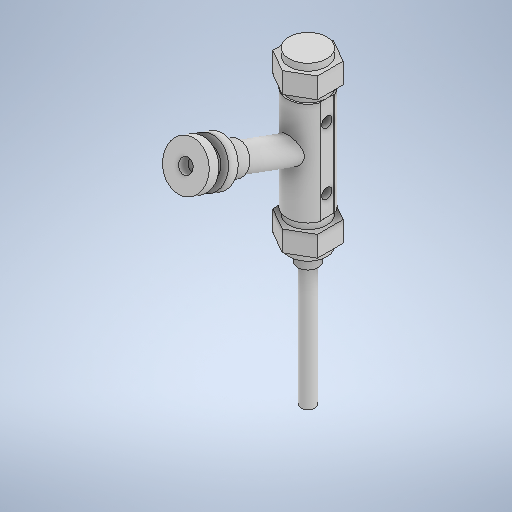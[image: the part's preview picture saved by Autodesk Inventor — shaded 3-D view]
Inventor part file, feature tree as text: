
AUTODESK INVENTOR PART (.ipt)
format: ipt  version: 2025.1 (Build 291241000, 241)  size: 469,504 bytes
history: native  units: mm
features: extrude x17, sketch x16, plane x13, other x6, hole x3, projected_geometry x3, mirror x2, shell x1, sweep x1, split x1, surface_op x1
ambient origin geometry x8: Origin, YZ Plane, XZ Plane, XY Plane, X Axis, Y Axis, Z Axis, Center Point
bodies: Volumenkörper1 (feature_tree), Solid3 (feature_tree), Solid4 (feature_tree), Solid5 (feature_tree), Solid6 (feature_tree), Solid7 (feature_tree), Solid8 (feature_tree), Solid9 (feature_tree), Solid10 (feature_tree), Solid11 (feature_tree), Solid12 (feature_tree), Solid13 (feature_tree)
feature tree (64):
  extrude  "Extrusion1"  TaperAngle=0.0deg  [1 undecoded]
  plane  "Arbeitsebene1"
  extrude  "Extrusion2"  Depth=50.0mm TaperAngle=0.0deg
  plane  "Arbeitsebene2"
  extrude  "Extrusion4"  Depth=12.0mm
  mirror  "Spiegeln1"
  extrude  "Extrusion5"  Depth=6.0mm TaperAngle=0.0deg
  hole  "Bohrung1"  [1 undecoded]
  mirror  "Spiegeln2"
  plane  "Work Plane6"
  extrude  "Extrusion6"  Depth=9.0mm
  hole  "Hole2"  [1 undecoded]
  extrude  "Extrusion7"  Depth=6.0mm TaperAngle=0.0deg
  shell  "Shell1"  Thickness=4.0mm
  plane  "Work Plane16"
  sketch  "Sketch21"  dims[d71=4.0mm d72=6.0mm d73=4.0mm d74=2.0mm d75=90.0deg d76=10.0mm d77=0.0mm d78=4.0mm]
  other  "Work Point4"
  other  "Work Point5"
  plane  "Work Plane17"
  sketch  "Sketch22"  dims[d79=46.0mm d80=0.0mm d81=0.25mm]
  other  "Work Point6"
  other  "Work Point7"
  plane  "Work Plane18"
  plane  "Work Plane19"
  plane  "Work Plane21"
  sketch  "Sketch25"  dims[d88=16.2mm d89=18.0mm]
  plane  "Work Plane24"
  extrude  "Extrusion9"  Depth=0.25mm
  extrude  "Extrusion14"  Depth=12.217305mm
  extrude  "Extrusion15"  Depth=12.0mm
  extrude  "Extrusion16"  Depth=18.0mm
  extrude  "Extrusion17"  Depth=2.0mm
  hole  "Hole3"  [1 undecoded]
  extrude  "Extrusion18"  Depth=15.0mm
  extrude  "Extrusion10"  TaperAngle=0.0deg  [1 undecoded]
  extrude  "Extrusion11"  Depth=15.0mm
  extrude  "Extrusion12"  Depth=46.0mm TaperAngle=0.0deg
  extrude  "Extrusion13"  Depth=15.0mm
  plane  "Work Plane20"
  extrude  "Extrusion8"  Depth=6.0mm
  sweep  "Sweep5"
  split  "Split1"
  plane  "Work Plane12"
  sketch  "Sketch19"  dims[d68=6.0mm d69=4.0mm d70=0.0mm]
  sketch  "Skizze1"  dims[d1=30.0mm d2=0.0mm d3=0.0mm]
  sketch  "Skizze2"  dims[d4=11.0mm d5=50.0mm d6=0.0mm]
  sketch  "Skizze4"  dims[d7=2.0mm d10=12.0mm]
  projected_geometry  "Projizierte Kontur1"
  sketch  "Skizze6"  dims[d11=15.0mm d12=6.0mm d13=0.0mm]
  sketch  "Skizze7"  dims[d16=0.5mm d17=4.0mm]
  sketch  "Sketch15"  dims[d18=6.0mm d19=0.0mm]
  sketch  "Sketch16"  dims[d20=3.0mm d21=6.0mm d22=4.0mm d23=2.0mm d24=90.0deg d25=18.0mm d26=0.0mm d27=9.0mm]
  sketch  "Sketch17"  dims[d28=18.0mm d48=0.0mm]
  other  "Tube 142"
  sketch  "Sketch23"  dims[d84=0.0mm d85=12.217305mm]
  sketch  "Sketch24"  dims[d86=18.0mm d87=12.0mm]
  plane  "Work Plane22"
  plane  "Work Plane23"
  sketch  "Sketch26"  dims[d92=2.0mm d94=8.5mm]
  sketch  "Sketch28"  dims[d96=0.0mm d97=12.217305mm d98=11.0mm d99=0.0mm d100=0.0mm d101=11.0mm d102=46.0mm d103=0.0mm d104=16.5mm d105=6.0mm d106=3.0mm d107=3.0mm d108=10.0mm d109=0.0mm d110=10.0mm d111=0.0mm d112=10.0mm d113=0.0mm d114=10.0mm d115=0.0mm d116=4.0mm d117=0.0mm d118=6.0mm d119=0.0mm d120=3.0mm d121=0.0mm d122=3.0mm d123=0.0mm d124=3.0mm d125=0.0mm d126=4.0mm d127=6.0mm d128=4.0mm d129=2.0mm d130=90.0deg d131=10.0mm d132=0.0mm d133=15.0mm d134=0.0mm]
  surface_op  "Surface1"
  projected_geometry  "Project Cut Edges1"
  projected_geometry  "Project Cut Edges2"
  other  "Srf1"
note: 5 required parameter values undecoded (feature->parameter linkage not recoverable at this tier; creation-order binding heuristic only, values carry confidence <= 0.55)
